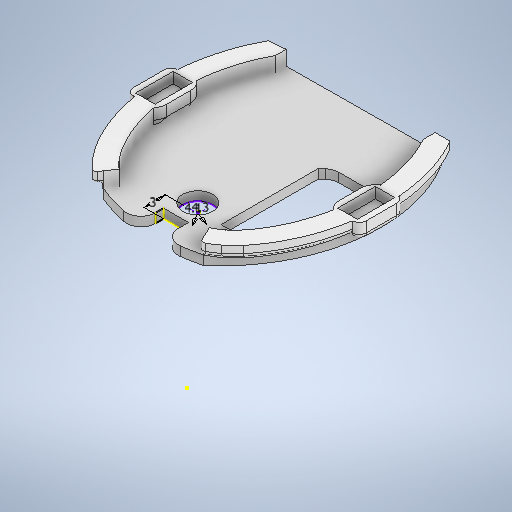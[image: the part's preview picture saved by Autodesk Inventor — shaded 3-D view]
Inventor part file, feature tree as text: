
AUTODESK INVENTOR PART (.ipt)
format: ipt  version: 2025.4 (Build 294407000, 407)  size: 700,928 bytes
history: native  units: in
note: dims shown in document units (in); Inventor stores cm internally (conversion verified against a paired STEP export)
features: sketch x10, fillet x9, extrude x7, other x3
ambient origin geometry x8: Origin, YZ Plane, XZ Plane, XY Plane, X Axis, Y Axis, Z Axis, Center Point
bodies: Solid1 (feature_tree), Solid2 (feature_tree)
feature tree (29):
  other  "rat_cap_EC_v12.iam"
  other  "rat_cap_walls_v8.iam:1::rat_cap_left_wall_v8.ipt:1"
  other  "rat_cap_walls_v8.iam:1::rat_cap_right_wall_v8.ipt:1"
  extrude  "Extrusion1"  Depth=0.3937in TaperAngle=0.0deg
  sketch  "Sketch3"  dims[d16=0.315in d17=0.0812in d18=0.0in]
  extrude  "Extrusion4"  Depth=0.0812in TaperAngle=0.0deg
  extrude  "Extrusion5"  Depth=0.0787in
  fillet  "Fillet5"  Radius=0.0787in
  fillet  "Fillet6"  Radius=0.0787in
  fillet  "Fillet7"  Radius=0.0787in
  fillet  "Fillet8"  Radius=0.0787in
  fillet  "Fillet10"  Radius=0.0787in
  fillet  "Fillet11"  Radius=0.0394in
  fillet  "Fillet12"  Radius=0.0787in
  sketch  "Sketch17"  dims[d79=0.05in d80=0.0in d81=0.1181in]
  extrude  "Extrusion16"  Depth=0.0394in
  fillet  "Fillet17"  Radius=0.0394in
  fillet  "Fillet18"  Radius=0.0197in
  extrude  "Extrusion17"  Depth=0.1181in
  extrude  "Extrusion19"  Depth=0.1614in
  sketch  "Sketch23"  dims[d35=0.0197in]
  sketch  "Sketch24"  dims[d36=0.0344in d58=0.0197in d59=0.0344in d60=0.0197in d61=0.0344in d75=0.0197in d76=0.0344in d77=0.0197in d78=0.0344in d88=0.0197in d89=0.0344in]
  extrude  "Extrusion21"  Depth=0.0197in
  sketch  "Sketch1"  dims[d0=0.3937in d1=0.05in d2=0.0in]
  sketch  "Sketch5"  dims[d19=0.0812in d20=0.0in d42=0.0787in d43=0.0787in d48=0.0787in d49=0.0787in d51=0.0787in d52=0.0787in d53=0.0394in d64=0.0787in]
  sketch  "Sketch6"  dims[d65=0.3878in d66=0.0in d67=0.0394in d68=0.0394in d72=0.0197in d73=0.0in]
  sketch  "Sketch18"  dims[d82=0.1693in d85=0.1614in]
  sketch  "Sketch19"  dims[d86=0.1339in d87=0.0in d33=0.0197in]
  sketch  "Sketch22"  dims[d34=0.0344in]
